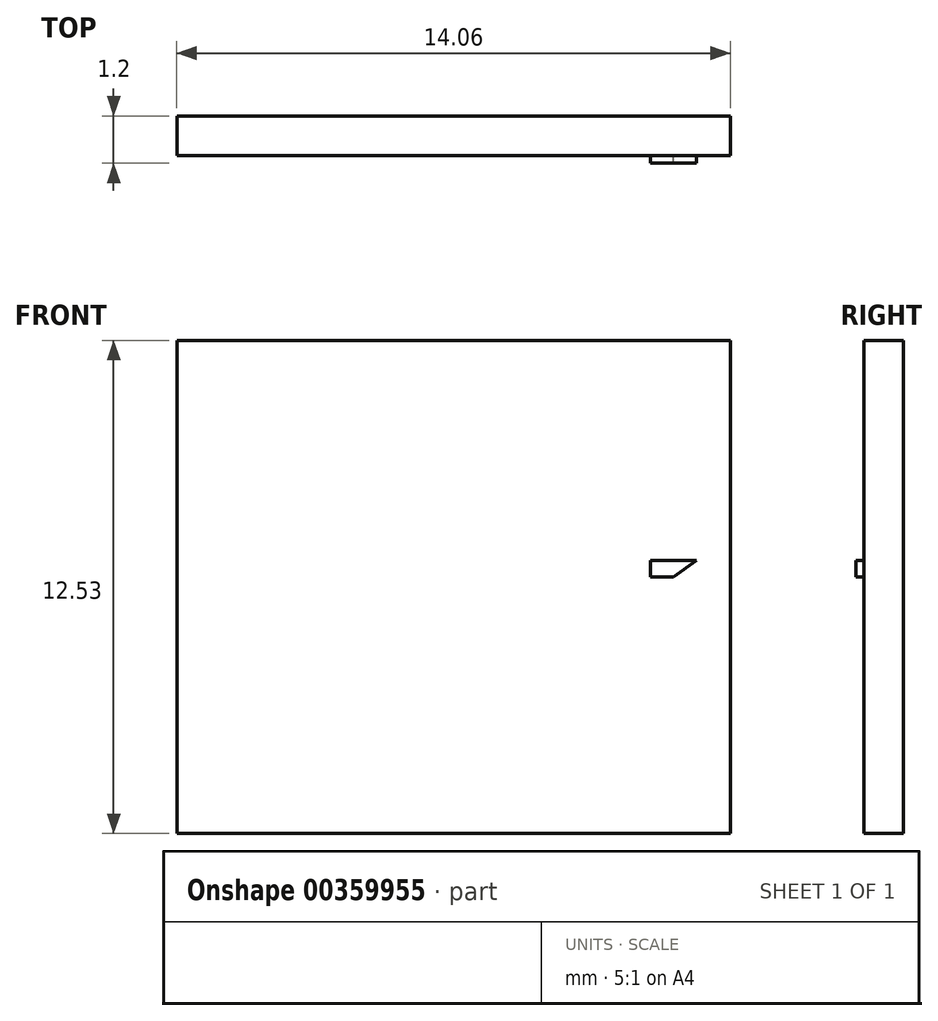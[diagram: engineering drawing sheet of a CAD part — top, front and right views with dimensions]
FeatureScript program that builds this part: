
annotation { "Feature Type Name" : "Feature", "Feature Type Description" : "" }
export const myFeature = defineFeature(function(context is Context, id is Id, definition is map)
    precondition{}
    {
        {
            var Q0;
            Q0=qCreatedBy(makeId("Front.planeOp"),FACE);
            var sketch = newSketch(context, id + "F0", { "sketchPlane" : qUnion([Q0])});
            skLineSegment(sketch, "E0.bottom", {"start": v(0, 12.53) * mm, "end": v(-14.06, 12.53) * mm});
            skLineSegment(sketch, "E0.top", {"start": v(0, 0) * mm, "end": v(-14.06, 0) * mm});
            skLineSegment(sketch, "E0.left", {"start": v(0, 12.53) * mm, "end": v(0, 0) * mm});
            skLineSegment(sketch, "E0.right", {"start": v(-14.06, 12.53) * mm, "end": v(-14.06, 0) * mm});
            skSolve(sketch);
        }
        {
            var Q0;
            Q0 = qSketchRegion(id + "F0", true);
            extrude(context, id + "F1", {"entities" : qUnion([Q0]), "depth" : 1 * mm});
        }
        {
            var Q0;
            Q0=makeQuery(id+"F1.opExtrude","CAP_FACE",FACE,{"disambiguationData":[OSD([sQuery(id+"F0.wireOp",EDGE,"E0.bottom"),sQuery(id+"F0.wireOp",EDGE,"E0.top"),sQuery(id+"F0.wireOp",EDGE,"E0.left"),sQuery(id+"F0.wireOp",EDGE,"E0.right")])],"isStart":false});
            var sketch = newSketch(context, id + "F2", { "sketchPlane" : qUnion([Q0])});
            skLineSegment(sketch, "E1", {"start": v(-0.85, 6.93) * mm, "end": v(-2.02, 6.93) * mm});
            skLineSegment(sketch, "E2", {"start": v(-2.02, 6.93) * mm, "end": v(-0.85, 6.93) * mm});
            skLineSegment(sketch, "E3", {"start": v(-2.02, 6.93) * mm, "end": v(-2.02, 6.51) * mm});
            skLineSegment(sketch, "E4", {"start": v(-2.02, 6.51) * mm, "end": v(-1.44, 6.51) * mm});
            skPoint(sketch, "E4.endSnap0", {"position": v(-1.44, 6.93) * mm});
            skLineSegment(sketch, "E5", {"start": v(-1.44, 6.51) * mm, "end": v(-0.85, 6.93) * mm});
            skSolve(sketch);
        }
        {
            var Q0;
            Q0 = qSketchRegion(id + "F2", true);
            extrude(context, id + "F3", {"entities" : qUnion([Q0]), "operationType" : NewBodyOperationType.ADD, "depth" : 0.2 * mm});
        }
    });
